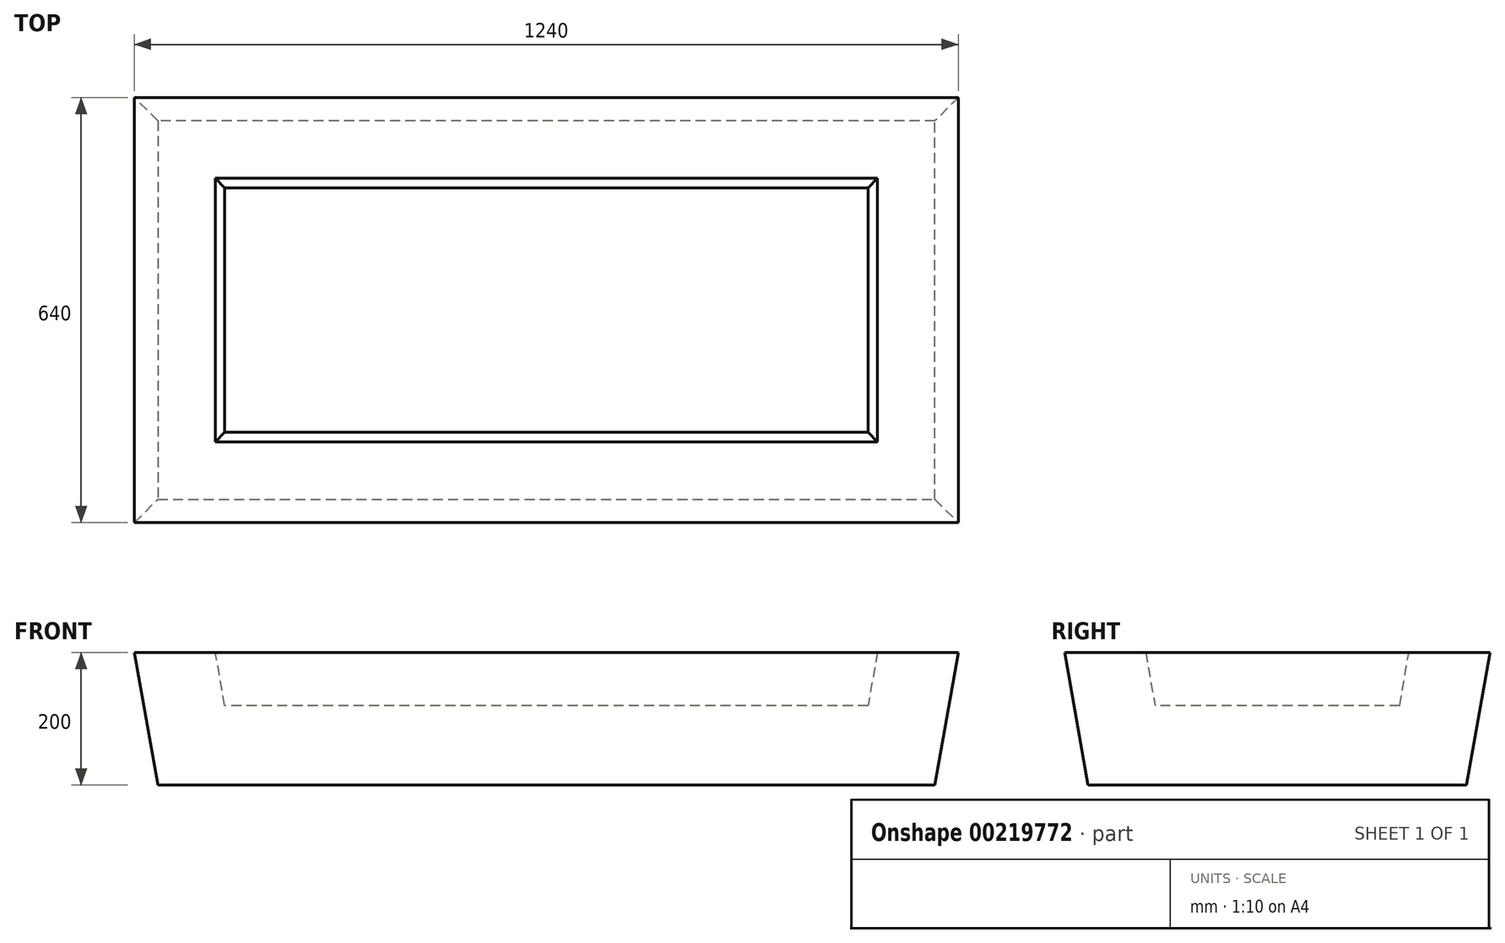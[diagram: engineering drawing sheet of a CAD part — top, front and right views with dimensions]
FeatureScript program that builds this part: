
annotation { "Feature Type Name" : "Feature", "Feature Type Description" : "" }
export const myFeature = defineFeature(function(context is Context, id is Id, definition is map)
    precondition{}
    {
        {
            var Q0;
            Q0=qCreatedBy(makeId("Top.planeOp"),FACE);
            var sketch = newSketch(context, id + "F0", { "sketchPlane" : qUnion([Q0])});
            skLineSegment(sketch, "E0.bottom", {"start": v(500, 200) * mm, "end": v(-500, 200) * mm});
            skLineSegment(sketch, "E0.top", {"start": v(500, -200) * mm, "end": v(-500, -200) * mm});
            skLineSegment(sketch, "E0.left", {"start": v(500, 200) * mm, "end": v(500, -200) * mm});
            skLineSegment(sketch, "E0.right", {"start": v(-500, 200) * mm, "end": v(-500, -200) * mm});
            skPoint(sketch, "E0.middle", {"position": v(0, 0) * mm});
            skLineSegment(sketch, "E1.0", {"start": v(-620, 320) * mm, "end": v(-620, -320) * mm});
            skLineSegment(sketch, "E1.1", {"start": v(620, 320) * mm, "end": v(-620, 320) * mm});
            skLineSegment(sketch, "E1.2", {"start": v(620, 320) * mm, "end": v(620, -320) * mm});
            skLineSegment(sketch, "E1.3", {"start": v(620, -320) * mm, "end": v(-620, -320) * mm});
            skSolve(sketch);
        }
        {
            var Q0;
            Q0=makeQuery(id+"F0.imprint","IMPRINT",FACE,{"disambiguationData":[TD([[makeQuery(id+"F0.imprint","IMPRINT",EDGE,{"derivedFrom":sQuery(id+"F0.wireOp",EDGE,"E0.bottom")}),-1.0]])]});
            var Q1;
            Q1=makeQuery(id+"F0.imprint","IMPRINT",FACE,{"disambiguationData":[TD([[makeQuery(id+"F0.imprint","IMPRINT",EDGE,{"derivedFrom":sQuery(id+"F0.wireOp",EDGE,"E0.bottom")}),1.0]])]});
            extrude(context, id + "F1", {"entities" : qUnion([Q0, Q1]), "oppositeDirection" : true, "depth" : 200 * mm, "hasDraft" : true, "draftAngle" : 10 * degree, "draftPullDirection" : true});
        }
        {
            var Q0;
            Q0=makeQuery(id+"F1.opExtrude","CAP_FACE",FACE,{"disambiguationData":[OSD([sQuery(id+"F0.wireOp",EDGE,"E1.0"),sQuery(id+"F0.wireOp",EDGE,"E1.1"),sQuery(id+"F0.wireOp",EDGE,"E1.2"),sQuery(id+"F0.wireOp",EDGE,"E1.3")])],"isStart":true});
            shell(context, id + "F2", {"entities" : qUnion([Q0]), "thickness" : 120 * mm});
        }
    });
